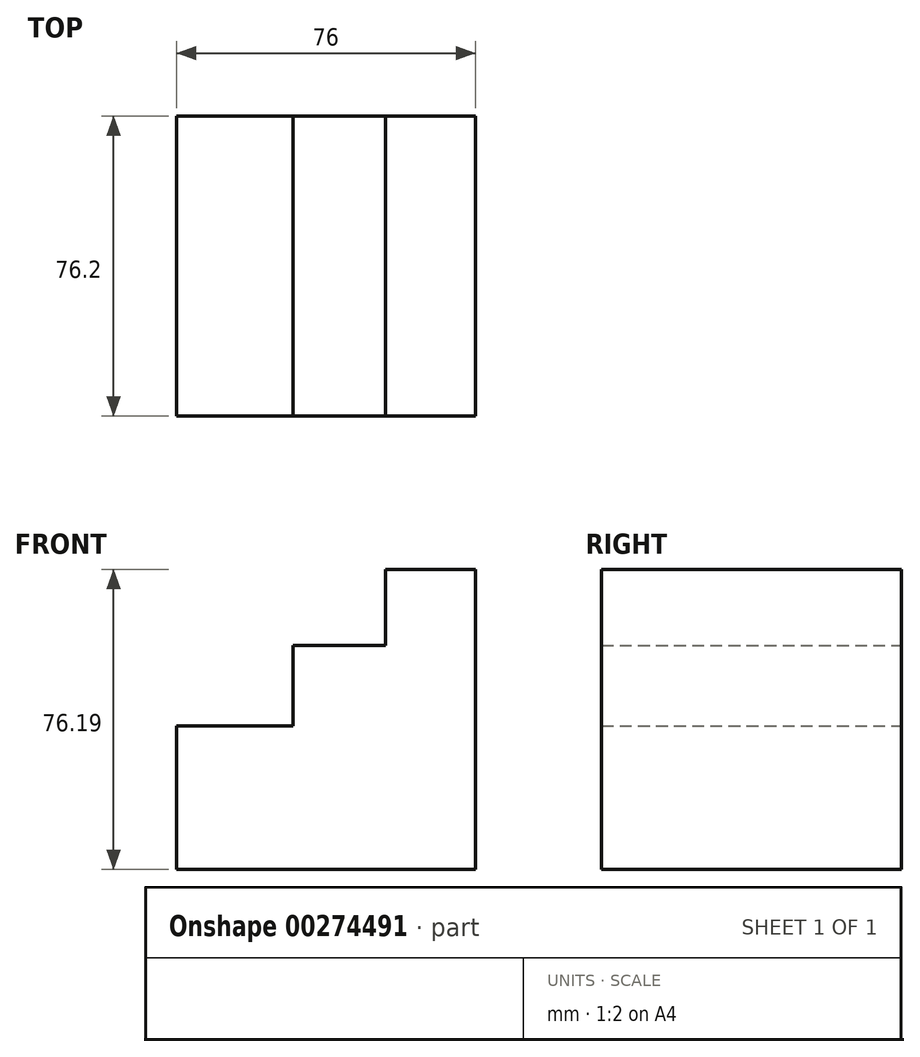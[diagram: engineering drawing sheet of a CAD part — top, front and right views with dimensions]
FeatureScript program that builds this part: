
annotation { "Feature Type Name" : "Feature", "Feature Type Description" : "" }
export const myFeature = defineFeature(function(context is Context, id is Id, definition is map)
    precondition{}
    {
        {
            var Q0;
            Q0=qCreatedBy(makeId("Front.planeOp"),FACE);
            var sketch = newSketch(context, id + "F0", { "sketchPlane" : qUnion([Q0])});
            skLineSegment(sketch, "E0", {"start": v(0, 0) * mm, "end": v(0, 76.2) * mm});
            skLineSegment(sketch, "E1", {"start": v(0, 76.2) * mm, "end": v(-22.91, 76.2) * mm});
            skLineSegment(sketch, "E2", {"start": v(-22.91, 76.2) * mm, "end": v(-22.91, 56.9) * mm});
            skLineSegment(sketch, "E3", {"start": v(-22.91, 56.9) * mm, "end": v(-46.4, 56.9) * mm});
            skLineSegment(sketch, "E4", {"start": v(-46.4, 56.9) * mm, "end": v(-46.4, 36.47) * mm});
            skLineSegment(sketch, "E5", {"start": v(-46.4, 36.47) * mm, "end": v(-76, 36.47) * mm});
            skLineSegment(sketch, "E6", {"start": v(-76, 36.47) * mm, "end": v(-76, 0) * mm});
            skLineSegment(sketch, "E7", {"start": v(-76, 0) * mm, "end": v(0, 0) * mm});
            skSolve(sketch);
        }
        {
            var Q0;
            Q0=makeQuery(id+"F0.imprint","IMPRINT",FACE,{"disambiguationData":[TD([[makeQuery(id+"F0.imprint","IMPRINT",EDGE,{"derivedFrom":sQuery(id+"F0.wireOp",EDGE,"E0")}),1.0]])]});
            extrude(context, id + "F1", {"entities" : qUnion([Q0]), "depth" : 76.2 * mm});
        }
    });
